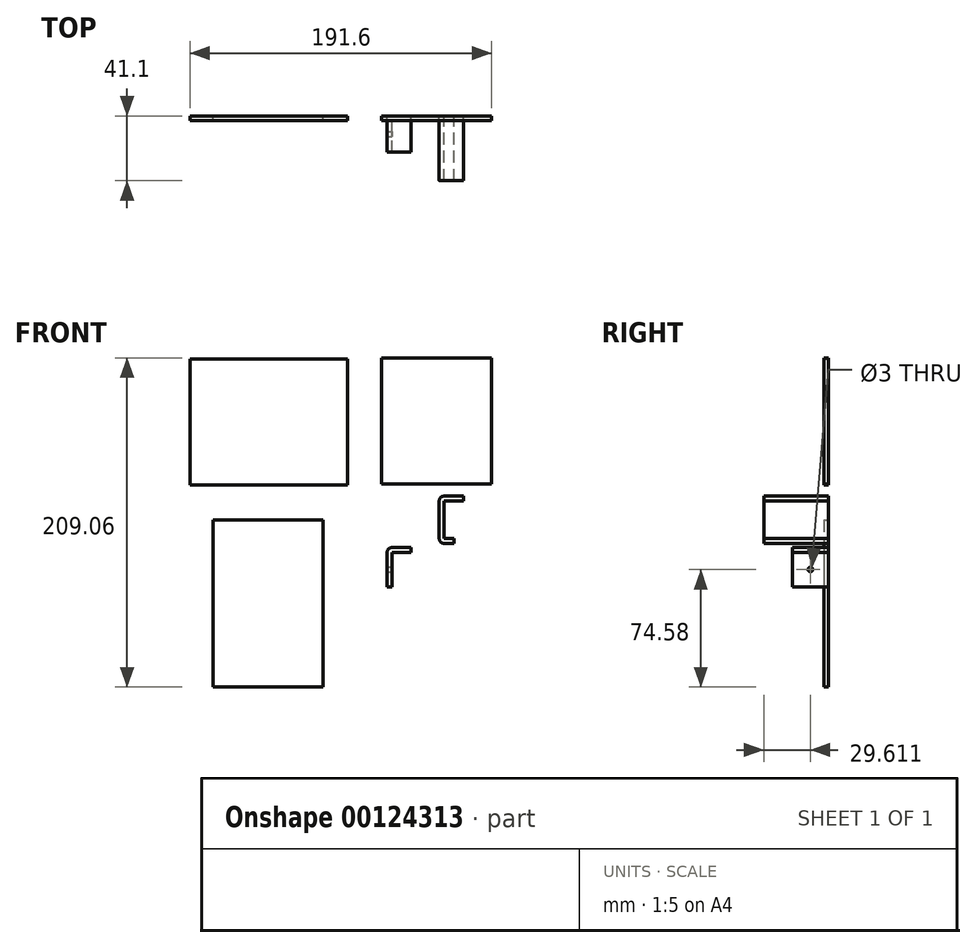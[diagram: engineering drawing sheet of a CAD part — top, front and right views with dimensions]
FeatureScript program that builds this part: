
annotation { "Feature Type Name" : "Feature", "Feature Type Description" : "" }
export const myFeature = defineFeature(function(context is Context, id is Id, definition is map)
    precondition{}
    {
        {
            var Q0;
            Q0=qCreatedBy(makeId("Front.planeOp"),FACE);
            var sketch = newSketch(context, id + "F0", { "sketchPlane" : qUnion([Q0])});
            skLineSegment(sketch, "E0.bottom", {"start": v(-14.85, 52.17) * mm, "end": v(55.15, 52.17) * mm});
            skLineSegment(sketch, "E0.top", {"start": v(-14.85, -27.83) * mm, "end": v(55.15, -27.83) * mm});
            skLineSegment(sketch, "E0.left", {"start": v(-14.85, 52.17) * mm, "end": v(-14.85, -27.83) * mm});
            skLineSegment(sketch, "E0.right", {"start": v(55.15, 52.17) * mm, "end": v(55.15, -27.83) * mm});
            skLineSegment(sketch, "E1.bottom", {"start": v(-136.45, 51.53) * mm, "end": v(-36.45, 51.53) * mm});
            skLineSegment(sketch, "E1.top", {"start": v(-136.45, -28.47) * mm, "end": v(-36.45, -28.47) * mm});
            skLineSegment(sketch, "E1.left", {"start": v(-136.45, 51.53) * mm, "end": v(-136.45, -28.47) * mm});
            skLineSegment(sketch, "E1.right", {"start": v(-36.45, 51.53) * mm, "end": v(-36.45, -28.47) * mm});
            skLineSegment(sketch, "E2.bottom", {"start": v(-51.95, -50.9) * mm, "end": v(-121.95, -50.9) * mm});
            skLineSegment(sketch, "E2.top", {"start": v(-51.95, -156.9) * mm, "end": v(-121.95, -156.9) * mm});
            skLineSegment(sketch, "E2.left", {"start": v(-51.95, -50.9) * mm, "end": v(-51.95, -156.9) * mm});
            skLineSegment(sketch, "E2.right", {"start": v(-121.95, -50.9) * mm, "end": v(-121.95, -156.9) * mm});
            skPoint(sketch, "E2.middle", {"position": v(-86.95, -103.9) * mm});
            skLineSegment(sketch, "E3.top", {"start": v(-11.25, -93.37) * mm, "end": v(-8.25, -93.37) * mm});
            skLineSegment(sketch, "E4.right", {"start": v(4.01, -68.37) * mm, "end": v(4.01, -71.37) * mm});
            skArc(sketch, "E5", {"start": v(-8.25, -68.37) * mm, "mid": v(-10.37, -69.25) * mm, "end": v(-11.25, -71.37) * mm});
            skLineSegment(sketch, "E6", {"start": v(-8.25, -68.37) * mm, "end": v(4.01, -68.37) * mm});
            skLineSegment(sketch, "E7", {"start": v(-11.25, -71.37) * mm, "end": v(-11.25, -93.37) * mm});
            skLineSegment(sketch, "E8", {"start": v(-8.25, -71.37) * mm, "end": v(4.01, -71.37) * mm});
            skLineSegment(sketch, "E9", {"start": v(-8.25, -71.37) * mm, "end": v(-8.25, -93.37) * mm});
            skLineSegment(sketch, "E10.right", {"start": v(37.08, -35.7) * mm, "end": v(37.08, -38.7) * mm});
            skLineSegment(sketch, "E11.right", {"start": v(31.33, -65.7) * mm, "end": v(31.33, -62.7) * mm});
            skLineSegment(sketch, "E12", {"start": v(24.82, -38.7) * mm, "end": v(24.82, -62.7) * mm});
            skLineSegment(sketch, "E13", {"start": v(24.82, -62.7) * mm, "end": v(31.33, -62.7) * mm});
            skLineSegment(sketch, "E14", {"start": v(24.82, -38.7) * mm, "end": v(37.08, -38.7) * mm});
            skLineSegment(sketch, "E15", {"start": v(24.82, -35.7) * mm, "end": v(37.08, -35.7) * mm});
            skLineSegment(sketch, "E16", {"start": v(21.82, -38.7) * mm, "end": v(21.82, -62.7) * mm});
            skLineSegment(sketch, "E17", {"start": v(24.82, -65.7) * mm, "end": v(31.33, -65.7) * mm});
            skArc(sketch, "E18", {"start": v(24.82, -35.7) * mm, "mid": v(22.7, -36.58) * mm, "end": v(21.82, -38.7) * mm});
            skArc(sketch, "E19", {"start": v(21.82, -62.7) * mm, "mid": v(22.7, -64.82) * mm, "end": v(24.82, -65.7) * mm});
            skSolve(sketch);
        }
        {
            var Q0;
            Q0=makeQuery(id+"F0.imprint","IMPRINT",FACE,{"disambiguationData":[TD([[makeQuery(id+"F0.imprint","IMPRINT",EDGE,{"derivedFrom":sQuery(id+"F0.wireOp",EDGE,"E0.bottom")}),-1.0]])]});
            extrude(context, id + "F1", {"entities" : qUnion([Q0]), "depth" : 3 * mm});
        }
        {
            var Q0;
            Q0 = qSketchRegion(id + "F0", true);
            extrude(context, id + "F2", {"entities" : qUnion([Q0]), "operationType" : NewBodyOperationType.ADD, "depth" : 3 * mm});
        }
        {
            var Q0;
            Q0=makeQuery(id+"F2.opExtrude","CAP_FACE",FACE,{"disambiguationData":[OSD([sQuery(id+"F0.wireOp",EDGE,"E3.top"),sQuery(id+"F0.wireOp",EDGE,"E4.right"),sQuery(id+"F0.wireOp",EDGE,"E5"),sQuery(id+"F0.wireOp",EDGE,"E6"),sQuery(id+"F0.wireOp",EDGE,"E7"),sQuery(id+"F0.wireOp",EDGE,"E8"),sQuery(id+"F0.wireOp",EDGE,"E9")])],"isStart":false});
            extrude(context, id + "F3", {"entities" : qUnion([Q0]), "operationType" : NewBodyOperationType.ADD, "depth" : 20 * mm});
        }
        {
            var Q0;
            Q0=qCreatedBy(makeId("Right.planeOp"),FACE);
            var sketch = newSketch(context, id + "F4", { "sketchPlane" : qUnion([Q0])});
            skCircle(sketch, "E20", {"center": v(-11.49, -82.3) * mm, "radius": 1.5 * mm});
            skSolve(sketch);
        }
        {
            var Q0;
            Q0=makeQuery(id+"F4.imprint","IMPRINT",FACE,{"disambiguationData":[TD([[makeQuery(id+"F4.imprint","IMPRINT",EDGE,{"derivedFrom":sQuery(id+"F4.wireOp",EDGE,"E20")}),1.0]])]});
            extrude(context, id + "F5", {"entities" : qUnion([Q0]), "operationType" : NewBodyOperationType.REMOVE, "oppositeDirection" : true, "depth" : 25.4 * mm});
        }
        {
            var Q0;
            Q0=makeQuery(id+"F2.opExtrude","CAP_FACE",FACE,{"disambiguationData":[OSD([sQuery(id+"F0.wireOp",EDGE,"E10.right"),sQuery(id+"F0.wireOp",EDGE,"E11.right"),sQuery(id+"F0.wireOp",EDGE,"E12"),sQuery(id+"F0.wireOp",EDGE,"E13"),sQuery(id+"F0.wireOp",EDGE,"E14"),sQuery(id+"F0.wireOp",EDGE,"E15"),sQuery(id+"F0.wireOp",EDGE,"E16"),sQuery(id+"F0.wireOp",EDGE,"E17"),sQuery(id+"F0.wireOp",EDGE,"E18"),sQuery(id+"F0.wireOp",EDGE,"E19")])],"isStart":false});
            extrude(context, id + "F6", {"entities" : qUnion([Q0]), "operationType" : NewBodyOperationType.ADD, "depth" : 38.1 * mm});
        }
    });
